# Revit family: _Grifería Sfera
name_source: partatom
category: Plumbing Fixtures
units: mm (PartAtom-declared; Revit-internal decimal feet)

## family parameters
Always vertical = Yes
Cut with Voids When Loaded = No
OmniClass Number = 23.31.11.00
OmniClass Title = Faucets
Part Type = Normal
Room Calculation Point = No
Round Connector Dimension = Use Diameter
Shared = No
Work Plane-Based = No

## types (1)
- _Grifería Sfera
    Aireador = tipo intercambiable con herramienta especial
    Aislante y anclaje = POM + FV
    Alto = 150 mm
    Ancho = 58 mm
    Cajas de control y baterías = ABS
    Ciclo de vida baterías = más de 500,000 activaciones
    Ciclo de vida de la unidad de cierre = 700.000 ciclos
    Creado por = IDD
    Description = Consumo máximo de 1.14 lpm Grifería electrónica activada por sensor capacitivo.
• Esfera de sensado de 10cm al rededor del cuerpo de la grifería. Posee aireador antivandálico y un anclaje de polímeros de alta ingeniería. No requiere puntoelectrico funciona mediante un pack de baterias Corona
    Diametro de acople para la conexión = G 1/2
    Fecha de creación = 27/07/2020
    Flujo Máximo = 1.14 L/min
    Manufacturer = Corona
    Material = Corona_Laton
    Material 2 = Corona_POM
    Peso Bruto aprox = 2400gr. / 5,29Lb
    Peso Neto aprox = 2140gr. / 4,72Lb.
    Presion maxima = 125 Psi (8.6 bar)
    Presion minima = 20 Psi (1.4 bar)
    Profundidad = 170 mm
    Protección de cables y baterías = IP64
    Temperaturas máxima de trabajo = 30ºC / 159,8 ºF (exclusivo para agua fría)
    Temperaturas mínima de trabajo = 2ºC / 41 ºF
    Voltaje = DC 7,2V

## geometry (parser evidence)
native form markers: Sweep x4
no freeform markers — native parametric forms only
